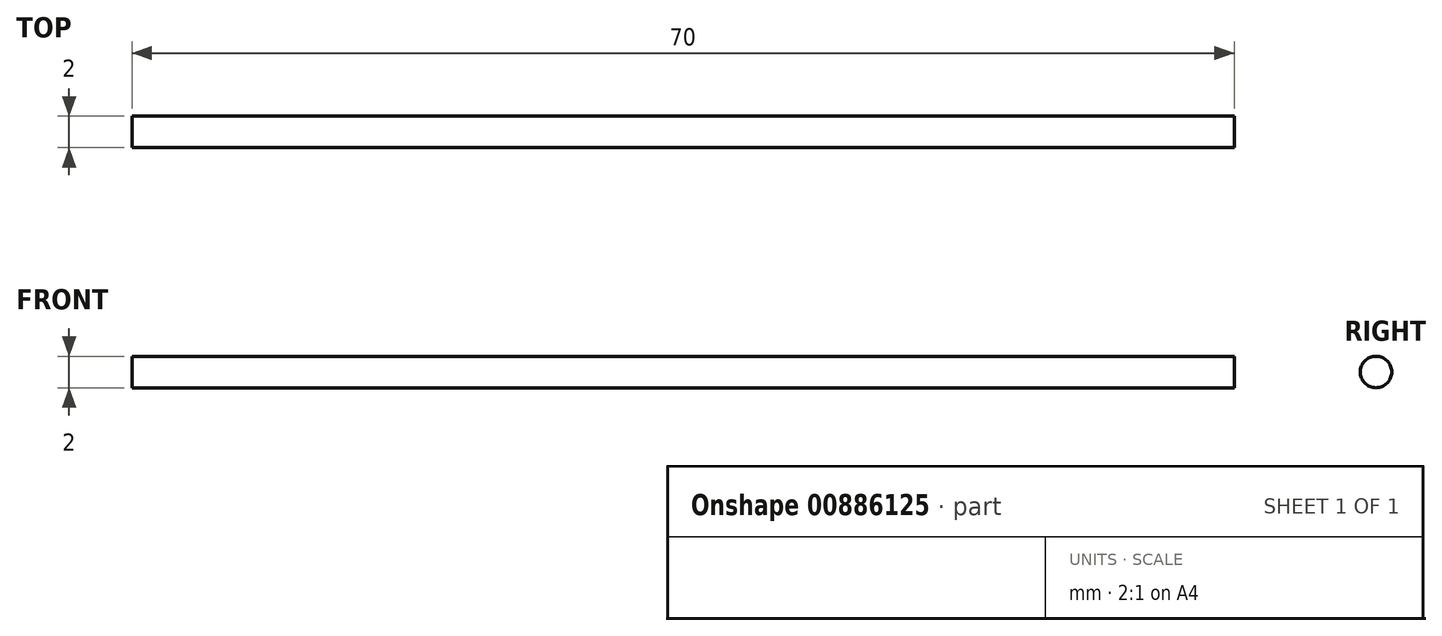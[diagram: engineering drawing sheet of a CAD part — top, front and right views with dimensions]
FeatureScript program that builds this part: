
annotation { "Feature Type Name" : "Feature", "Feature Type Description" : "" }
export const myFeature = defineFeature(function(context is Context, id is Id, definition is map)
    precondition{}
    {
        {
            var Q0;
            Q0=qCreatedBy(makeId("Right.planeOp"),FACE);
            var sketch = newSketch(context, id + "F0", { "sketchPlane" : qUnion([Q0])});
            skCircle(sketch, "E0", {"center": v(0, 0) * mm, "radius": 1 * mm});
            skSolve(sketch);
        }
        {
            var Q0;
            Q0 = qSketchRegion(id + "F0", true);
            extrude(context, id + "F1", {"entities" : qUnion([Q0]), "depth" : 70 * mm, "offsetDistance" : 25 * mm});
        }
    });
